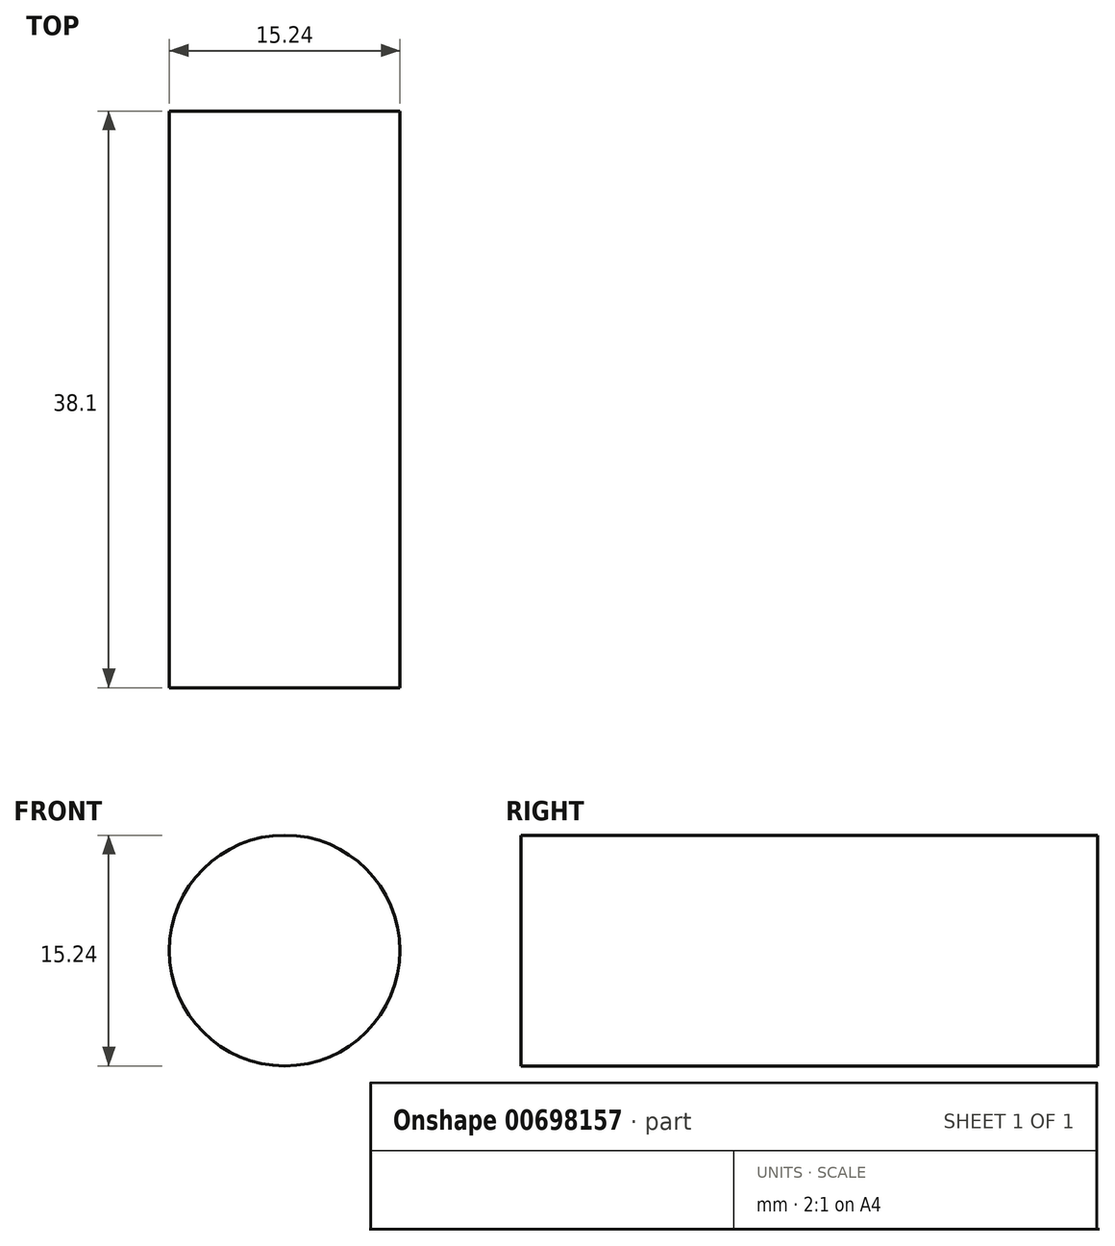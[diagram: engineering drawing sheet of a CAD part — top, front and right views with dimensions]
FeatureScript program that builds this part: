
annotation { "Feature Type Name" : "Feature", "Feature Type Description" : "" }
export const myFeature = defineFeature(function(context is Context, id is Id, definition is map)
    precondition{}
    {
        {
            var Q0;
            Q0=qCreatedBy(makeId("Front.planeOp"),FACE);
            var sketch = newSketch(context, id + "F0", { "sketchPlane" : qUnion([Q0])});
            skCircle(sketch, "E0", {"center": v(0, 0) * mm, "radius": 7.62 * mm});
            skSolve(sketch);
        }
        {
            var Q0;
            Q0=qSketchRegion(id+"F0",true);
            extrude(context, id + "F1", {"entities" : qUnion([Q0]), "depth" : 38.1 * mm, "offsetDistance" : 25.4 * mm});
        }
    });
